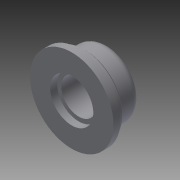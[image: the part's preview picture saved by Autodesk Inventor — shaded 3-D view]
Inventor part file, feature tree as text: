
AUTODESK INVENTOR PART (.ipt)
format: ipt  version: 2014 (Build 180170000, 170)  size: 131,072 bytes
history: native  units: mm
features: extrude x5, sketch x5, fillet x1, chamfer x1
ambient origin geometry x8: Origin, YZ Plane, XZ Plane, XY Plane, X Axis, Y Axis, Z Axis, Center Point
bodies: Solid1 (feature_tree)
feature tree (12):
  extrude  "Extrusion1"  Depth=2.0mm TaperAngle=0.0deg
  extrude  "Extrusion2"  Depth=6.5mm TaperAngle=0.0deg
  fillet  "Fillet1"  Radius=2.0mm
  extrude  "Extrusion3"  Depth=2.0mm TaperAngle=0.0deg
  chamfer  "Chamfer1"  Distance=0.5mm Angle=45.0deg
  extrude  "Extrusion4"  Depth=10.0mm TaperAngle=0.0deg
  extrude  "Extrusion5"  Depth=2.0mm TaperAngle=0.0deg
  sketch  "Sketch1"  dims[d0=22.0mm d1=2.0mm d2=0.0mm]
  sketch  "Sketch2"  dims[d3=18.5mm d4=6.5mm d5=0.0mm d6=2.0mm]
  sketch  "Sketch3"  dims[d7=24.0mm d8=2.0mm d9=0.0mm d10=0.5mm d11=2.0mm d12=45.0deg]
  sketch  "Sketch4"  dims[d13=10.0mm d14=10.0mm d15=0.0mm]
  sketch  "Sketch5"  dims[d16=12.4mm d17=2.0mm d18=0.0mm]
